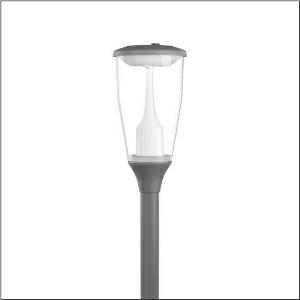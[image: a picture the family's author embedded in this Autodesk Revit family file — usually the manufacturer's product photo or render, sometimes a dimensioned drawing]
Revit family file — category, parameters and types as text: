
# Revit family: dl_11_iq___st1_2a_5xa5575ev14h000022_9f00
name_source: partatom
category: Lighting Fixtures
units: mm (PartAtom-declared; Revit-internal decimal feet)

## family parameters
Cut with Voids When Loaded = No
Host = Face
Light Source = No
Part Type = Normal
Room Calculation Point = No
Round Connector Dimension = Use Diameter
Shared = No

## types (1)
- --- (1 x LED, 1560 lm, 10.7 W, 3000K)
    Apparent Load = 11 VA
    CIE Flux Codes = 24 63 94 96 100
    Color Rendering = 70
    Color Temperature = 3000K
    Default Elevation = 1800 mm
    Description = DL 11 iQ, mast luminaire, Module 540 iQ-SR, primary light control with 3 zone facetted reflector, of plastic, silver coated, highly specular, structured, primary optical cover: cover, of PMMA, transparent, light distribution: ST1.2a, light emission: direct distribution, primary light characteristic: asymmetric, installation type: post-top, LED, High Power LED, rated luminous flux: 1.560lm, luminous efficacy: 146lm/W, light colour: 730, colour temperature: 3000K, control gear: iQ-Street Remote, D4i with power reduction, control: pre-setting: logarithmic dimming characteristic, Street-Remote, Auto-Match, Temp-Guard, Lumen-Switch, Night-Set, Smart-Wire, Light-Fading, Desk-Remote (wireless, voltage-free reading and setting of iQ features in the workshop via application-optimized NFC function/RFID function), optimised constant luminous flux control (CLO 2.0), mains connection: 220..240V, AC, 50/60Hz, connection cable pre-assembled, cable length: 5,5m, start of lifetime: 11W, end of service life: 11W, reduction: 6W, luminaire housing, upper part, of diecast aluminium, coated, Siteco® metallic grey (DB 702S), spigot size: 76mm (post-top), mounting height: 3..5m, post-top mast mounting element, of diecast aluminium, coated, Siteco® metallic grey (DB 702S), Module 540 iQ-SR, traffic white (RAL 9016), equipment: standard, Smart Interface above, protection rating (complete): IP66, insulation class (complete): insulation class II (safety insulation), certification: CE, ENEC, ENEC+, VDE, impact resistance: IK07, packaging unit: 1 piece

Light Distribution: ST1.2a
    Height = 665 mm
    Lamp = 1 x LED
    Lamp Light Flux = 1560 lm
    Lamp Power = 10.7 W
    Lamp count = 1
    Length = 334 mm
    Luminous efficacy = 146 lm/W
    Manufacturer = Siteco
    ModVariant = No
    Model = 5XA5575EV14H000022
    Number of Poles = 1
    OnlyDefault = Yes
    Power Factor = 1
    Product Name = DL 11 iQ | ST1.2a
    Product group = mast luminaire | pylon top
    ProductGroupID = 6100
    Protection Class = Protection class II
    Protection Degree = IP 66
    RLX_Detail_Level = 1
    RLX_Emergency_Light_Flux = 0 lm
    RLX_Emergency_Type = 0
    RLX_Emergency_Type_DB = No
    RlxData = <blob elided: 154357 chars, md5=6555f59f>
    Socket = socket
    Standby Power = 0 W
    System Light Flux = 1560 lm
    System Power = 11 W
    Type Comments = factory setting: luminous flux: 100 % | dim-lin: 254 | 419 mA
    Type Image = l_1337541.jpg
    URL = http://relux.com
    VarID = @adj_094760
    Voltage = 0 V
    Weight = 0.00 kg
    Width = 0 mm  [stored 0 ft]

note: [stored X ft] marks values corroborated as IEEE doubles in the binary element streams (Revit-internal decimal feet)

## geometry (parser evidence)
native form markers: Blend x4, Sweep x10
no freeform markers — native parametric forms only
